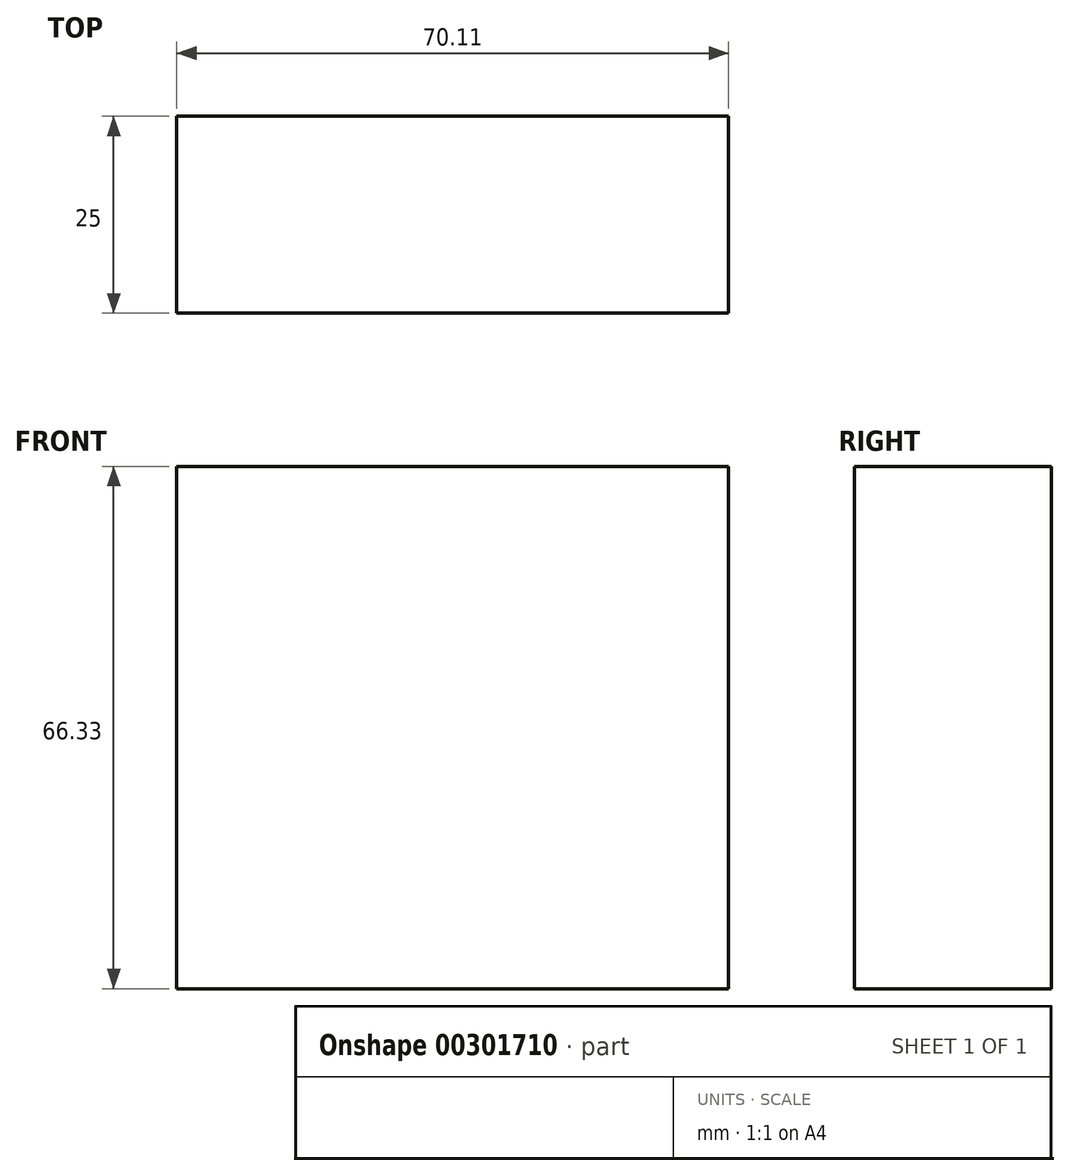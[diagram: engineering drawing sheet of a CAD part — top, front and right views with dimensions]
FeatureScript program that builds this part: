
annotation { "Feature Type Name" : "Feature", "Feature Type Description" : "" }
export const myFeature = defineFeature(function(context is Context, id is Id, definition is map)
    precondition{}
    {
        {
            var Q0;
            Q0=qCreatedBy(makeId("Front.planeOp"),FACE);
            var sketch = newSketch(context, id + "F0", { "sketchPlane" : qUnion([Q0])});
            skLineSegment(sketch, "E0.bottom", {"start": v(-130.8, -6.28) * mm, "end": v(-60.7, -6.28) * mm});
            skLineSegment(sketch, "E0.top", {"start": v(-130.8, 60.05) * mm, "end": v(-60.7, 60.05) * mm});
            skLineSegment(sketch, "E0.left", {"start": v(-130.8, -6.28) * mm, "end": v(-130.8, 60.05) * mm});
            skLineSegment(sketch, "E0.right", {"start": v(-60.7, -6.28) * mm, "end": v(-60.7, 60.05) * mm});
            skPoint(sketch, "E0.middle", {"position": v(-95.74, 26.89) * mm});
            skSolve(sketch);
        }
        {
            var Q0;
            Q0=makeQuery(id+"F0.imprint","IMPRINT",FACE,{"disambiguationData":[TD([[makeQuery(id+"F0.imprint","IMPRINT",EDGE,{"derivedFrom":sQuery(id+"F0.wireOp",EDGE,"E0.bottom")}),1.0]])]});
            extrude(context, id + "F1", {"entities" : qUnion([Q0]), "depth" : 25 * mm});
        }
    });
